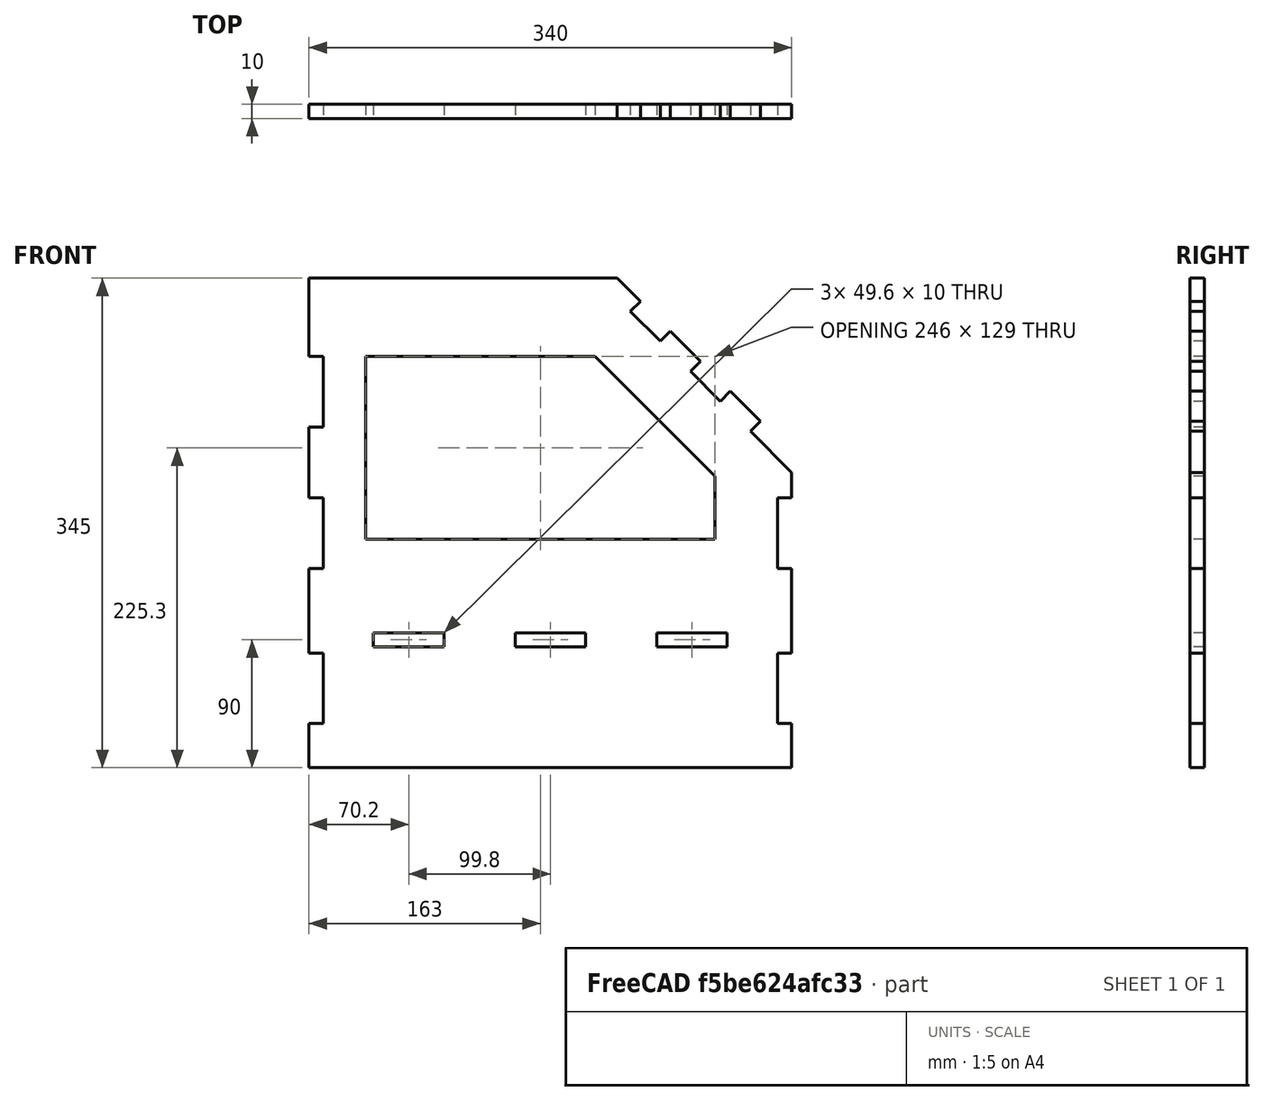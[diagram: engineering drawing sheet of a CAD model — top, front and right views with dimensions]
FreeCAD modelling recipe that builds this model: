
FCSTD DOCUMENT  (FreeCAD 0.19R19327 (Git))
Label: Lateral_izquierdo
License: All rights reserved
LicenseURL: http://en.wikipedia.org/wiki/All_rights_reserved
objects: Sketcher::SketchObject×1, PartDesign::Pad×1, PartDesign::Body×1
note: 4 computed .brp shape members not serialized (recipe doc carries the construction recipe); baked Part::Feature solids carry a one-line shape summary decoded from their .brp

FEATURE [Sketcher::SketchObject] Sketch
  MapMode = 5
  Placement = pos=(0,0,0) rot=(1,0,0;1.5708rad)
  Support = -> [XZ_Plane]
  sketch-geometry (57):
    g0: LineSegment StartX=0 StartY=0 StartZ=0 EndX=0 EndY=30.933 EndZ=0
    g1: LineSegment StartX=0 StartY=30.933 StartZ=0 EndX=10 EndY=30.933 EndZ=0
    g2: LineSegment StartX=10 StartY=30.933 StartZ=0 EndX=10 EndY=80.733 EndZ=0
    g3: LineSegment StartX=10 StartY=80.733 StartZ=0 EndX=0 EndY=80.733 EndZ=0
    g4: LineSegment StartX=0 StartY=80.733 StartZ=0 EndX=0 EndY=140.2 EndZ=0
    g5: LineSegment StartX=0 StartY=140.2 StartZ=0 EndX=10 EndY=140.2 EndZ=0
    g6: LineSegment StartX=10 StartY=140.2 StartZ=0 EndX=10 EndY=190 EndZ=0
    g7: LineSegment StartX=10 StartY=190 StartZ=0 EndX=0 EndY=190 EndZ=0
    g8: LineSegment StartX=-1e-16 StartY=190 StartZ=0 EndX=-1e-16 EndY=240 EndZ=0
    g9: LineSegment StartX=-1e-16 StartY=240 StartZ=0 EndX=10 EndY=240 EndZ=0
    g10: LineSegment StartX=10 StartY=240 StartZ=0 EndX=10 EndY=289.8 EndZ=0
    g11: LineSegment StartX=10 StartY=289.8 StartZ=0 EndX=0 EndY=289.8 EndZ=0
    g12: LineSegment StartX=0 StartY=289.8 StartZ=0 EndX=0 EndY=345 EndZ=0
    g13: LineSegment StartX=0 StartY=345 StartZ=0 EndX=217.071 EndY=345 EndZ=0
    g14: LineSegment StartX=217.071 StartY=345 StartZ=0 EndX=233.405 EndY=328.666 EndZ=0
    g15: LineSegment StartX=233.405 StartY=328.666 StartZ=0 EndX=226.334 EndY=321.595 EndZ=0
    g16: LineSegment StartX=226.334 StartY=321.595 StartZ=0 EndX=247.406 EndY=300.523 EndZ=0
    g17: LineSegment StartX=247.406 StartY=300.523 StartZ=0 EndX=254.477 EndY=307.594 EndZ=0
    g18: LineSegment StartX=254.477 StartY=307.594 StartZ=0 EndX=275.69 EndY=286.381 EndZ=0
    g19: LineSegment StartX=275.69 StartY=286.381 StartZ=0 EndX=268.619 EndY=279.31 EndZ=0
    g20: LineSegment StartX=268.619 StartY=279.31 StartZ=0 EndX=289.691 EndY=258.238 EndZ=0
    g21: LineSegment StartX=289.691 StartY=258.238 StartZ=0 EndX=296.762 EndY=265.309 EndZ=0
    g22: LineSegment StartX=296.762 StartY=265.309 StartZ=0 EndX=317.975 EndY=244.096 EndZ=0
    g23: LineSegment StartX=317.975 StartY=244.096 StartZ=0 EndX=310.904 EndY=237.025 EndZ=0
    g24: LineSegment StartX=310.904 StartY=237.025 StartZ=0 EndX=340 EndY=207.929 EndZ=0
    g25: LineSegment StartX=340 StartY=207.929 StartZ=0 EndX=340 EndY=190 EndZ=0
    g26: LineSegment StartX=340 StartY=190 StartZ=0 EndX=330 EndY=190 EndZ=0
    g27: LineSegment StartX=330 StartY=190 StartZ=0 EndX=330 EndY=140.2 EndZ=0
    g28: LineSegment StartX=330 StartY=140.2 StartZ=0 EndX=340 EndY=140.2 EndZ=0
    g29: LineSegment StartX=340 StartY=140.2 StartZ=0 EndX=340 EndY=80.733 EndZ=0
    g30: LineSegment StartX=340 StartY=80.733 StartZ=0 EndX=330 EndY=80.733 EndZ=0
    g31: LineSegment StartX=330 StartY=80.733 StartZ=0 EndX=330 EndY=30.933 EndZ=0
    g32: LineSegment StartX=330 StartY=30.933 StartZ=0 EndX=340 EndY=30.933 EndZ=0
    g33: LineSegment StartX=340 StartY=30.933 StartZ=0 EndX=340 EndY=0 EndZ=0
    g34: LineSegment StartX=340 StartY=0 StartZ=0 EndX=0 EndY=0 EndZ=0
    g35: LineSegment [constr] StartX=-6e-16 StartY=85 StartZ=0 EndX=340 EndY=85 EndZ=0
    g36: LineSegment StartX=45.4 StartY=85 StartZ=0 EndX=95 EndY=85 EndZ=0
    g37: LineSegment StartX=95 StartY=85 StartZ=0 EndX=95 EndY=95 EndZ=0
    g38: LineSegment StartX=95 StartY=95 StartZ=0 EndX=45.4 EndY=95 EndZ=0
    g39: LineSegment StartX=45.4 StartY=95 StartZ=0 EndX=45.4 EndY=85 EndZ=0
    g40: LineSegment StartX=145.2 StartY=85 StartZ=0 EndX=194.8 EndY=85 EndZ=0
    g41: LineSegment StartX=194.8 StartY=85 StartZ=0 EndX=194.8 EndY=95 EndZ=0
    g42: LineSegment StartX=194.8 StartY=95 StartZ=0 EndX=145.2 EndY=95 EndZ=0
    g43: LineSegment StartX=145.2 StartY=95 StartZ=0 EndX=145.2 EndY=85 EndZ=0
    g44: LineSegment StartX=245 StartY=85 StartZ=0 EndX=294.6 EndY=85 EndZ=0
    g45: LineSegment StartX=294.6 StartY=85 StartZ=0 EndX=294.6 EndY=95 EndZ=0
    g46: LineSegment StartX=294.6 StartY=95 StartZ=0 EndX=245 EndY=95 EndZ=0
    g47: LineSegment StartX=245 StartY=95 StartZ=0 EndX=245 EndY=85 EndZ=0
    g48: LineSegment [constr] StartX=95 StartY=95 StartZ=0 EndX=145.2 EndY=95 EndZ=0
    g49: LineSegment [constr] StartX=194.8 StartY=95 StartZ=0 EndX=245 EndY=95 EndZ=0
    g50: LineSegment [constr] StartX=45.4 StartY=95 StartZ=0 EndX=0 EndY=95 EndZ=0
    g51: LineSegment [constr] StartX=294.6 StartY=95 StartZ=0 EndX=340 EndY=95 EndZ=0
    g52: LineSegment StartX=40 StartY=289.8 StartZ=0 EndX=40 EndY=160.8 EndZ=0
    g53: LineSegment StartX=40 StartY=160.8 StartZ=0 EndX=286 EndY=160.8 EndZ=0
    g54: LineSegment StartX=286 StartY=160.8 StartZ=0 EndX=286 EndY=205.3 EndZ=0
    g55: LineSegment StartX=286 StartY=205.3 StartZ=0 EndX=201.5 EndY=289.8 EndZ=0
    g56: LineSegment StartX=201.5 StartY=289.8 StartZ=0 EndX=40 EndY=289.8 EndZ=0
  constraints (169):
    c: Coincident(g-1,g0)
    c: PointOnObject(g0,g-2)
    c: Coincident(g0,g1)
    c: Horizontal(g1)
    c: Coincident(g1,g2)
    c: Vertical(g2)
    c: Coincident(g2,g3)
    c: Horizontal(g3)
    c: Coincident(g3,g4)
    c: PointOnObject(g4,g-2)
    c: Coincident(g4,g5)
    c: Horizontal(g5)
    c: Coincident(g5,g6)
    c: Vertical(g6)
    c: Coincident(g6,g7)
    c: Horizontal(g7)
    c: Coincident(g7,g8)
    c: Vertical(g8)
    c: Coincident(g8,g9)
    c: Horizontal(g9)
    c: Coincident(g9,g10)
    c: Vertical(g10)
    c: Coincident(g10,g11)
    c: Horizontal(g11)
    c: Coincident(g11,g12)
    c: PointOnObject(g12,g-2)
    c: Coincident(g12,g13)
    c: Horizontal(g13)
    c: Coincident(g13,g14)
    c: Coincident(g14,g15)
    c: Coincident(g15,g16)
    c: Coincident(g16,g17)
    c: Coincident(g17,g18)
    c: Coincident(g18,g19)
    c: Coincident(g19,g20)
    c: Coincident(g20,g21)
    c: Coincident(g21,g22)
    c: Coincident(g22,g23)
    c: Coincident(g23,g24)
    c: Coincident(g24,g25)
    c: Coincident(g25,g26)
    c: Coincident(g26,g27)
    c: Coincident(g27,g28)
    c: Coincident(g28,g29)
    c: Vertical(g29)
    c: Coincident(g29,g30)
    c: Horizontal(g30)
    c: Coincident(g30,g31)
    c: Vertical(g31)
    c: Coincident(g31,g32)
    c: Horizontal(g32)
    c: Coincident(g32,g33)
    c: PointOnObject(g33,g-1)
    c: Coincident(g33,g34)
    c: Coincident(g34,g0)
    c: Horizontal(g26)
    c: Horizontal(g28)
    c: Vertical(g27)
    c: Vertical(g33)
    c: Equal(g1,g3)
    c: Equal(g3,g5)
    c: Equal(g5,g7)
    c: Equal(g7,g9)
    c: Equal(g9,g11)
    c: Equal(g11,g26)
    c: Equal(g26,g28)
    c: Equal(g28,g30)
    c: Equal(g30,g32)
    c: Equal(g32,g15)
    c: Equal(g15,g17)
    c: Equal(g17,g19)
    c: Equal(g19,g21)
    c: Equal(g21,g23)
    c: DistanceX(g1,g1) = 10
    c: Vertical(g25)
    c: Angle(g13,g14) = 2.35619
    c: Parallel(g16,g14)
    c: Parallel(g18,g16)
    c: Parallel(g20,g18)
    c: Parallel(g22,g20)
    c: Parallel(g24,g22)
    c: Perpendicular(g15,g14)
    c: Perpendicular(g16,g17)
    c: Perpendicular(g18,g19)
    c: Perpendicular(g20,g21)
    c: Perpendicular(g22,g23)
    c: Equal(g16,g20)
    c: Distance(g16) = 29.8
    c: Distance(g14) = 23.1
    c: Equal(g18,g22)
    c: Distance(g18) = 30
    c: Distance(g24) = 41.148
    c: DistanceX(g34,g34) = 340
    c: Equal(g2,g6)
    c: Equal(g6,g10)
    c: DistanceY(g10,g10) = 49.8
    c: DistanceY(g12,g12) = 55.2
    c: DistanceY(g0,g12) = 345
    c: Equal(g6,g27)
    c: Equal(g27,g31)
    c: DistanceY(g25,g25) = 17.929
    c: Equal(g33,g0)
    c: DistanceY(g0,g0) = 30.933
    c: DistanceY(g8,g8) = 50
    c: PointOnObject(g35,g4)
    c: PointOnObject(g35,g29)
    c: Horizontal(g35)
    c: Coincident(g36,g37)
    c: Coincident(g37,g38)
    c: Coincident(g38,g39)
    c: Coincident(g39,g36)
    c: Horizontal(g36)
    c: Horizontal(g38)
    c: Vertical(g37)
    c: Vertical(g39)
    c: PointOnObject(g36,g35)
    c: Coincident(g40,g41)
    c: Coincident(g41,g42)
    c: Coincident(g42,g43)
    c: Coincident(g43,g40)
    c: Horizontal(g40)
    c: Horizontal(g42)
    c: Vertical(g41)
    c: Vertical(g43)
    c: PointOnObject(g40,g35)
    c: Coincident(g44,g45)
    c: Coincident(g45,g46)
    c: Coincident(g46,g47)
    c: Coincident(g47,g44)
    c: Horizontal(g44)
    c: Horizontal(g46)
    c: Vertical(g45)
    c: Vertical(g47)
    c: PointOnObject(g44,g35)
    c: Equal(g39,g43)
    c: Equal(g43,g47)
    c: Equal(g38,g42)
    c: Equal(g42,g46)
    c: Coincident(g48,g37)
    c: Coincident(g48,g42)
    c: Coincident(g49,g41)
    c: Coincident(g49,g46)
    c: Equal(g48,g49)
    c: DistanceX(g38,g38) = 49.6
    c: DistanceY(g39,g39) = 10
    c: DistanceX(g48,g48) = 50.2
    c: Coincident(g50,g38)
    c: PointOnObject(g50,g4)
    c: Horizontal(g50)
    c: Coincident(g51,g45)
    c: PointOnObject(g51,g29)
    c: Horizontal(g51)
    c: Equal(g51,g50)
    c: DistanceY(g0,g35) = 85
    c: Vertical(g52)
    c: Coincident(g52,g53)
    c: Horizontal(g53)
    c: Coincident(g53,g54)
    c: Coincident(g54,g55)
    c: Coincident(g55,g56)
    c: Coincident(g56,g52)
    c: Horizontal(g56)
    c: Vertical(g54)
    c: DistanceX(g56,g56) = 161.5
    c: Parallel(g55,g20)
    c: DistanceY(g52,g52) = 129
    c: DistanceX(g0,g52) = 40
    c: DistanceY(g52,g12) = 55.2
    c: DistanceX(g53,g53) = 246
FEATURE [PartDesign::Pad] Pad
  Length = 10
  Length2 = 100
  Placement = pos=(0,0,0) rot=(1,0,0;1.5708rad)
  Profile = -> Sketch
  Type = 0
FEATURE [PartDesign::Body] Body
  Group = -> [Sketch,Pad]
  Origin = -> Origin
  Tip = -> Pad
